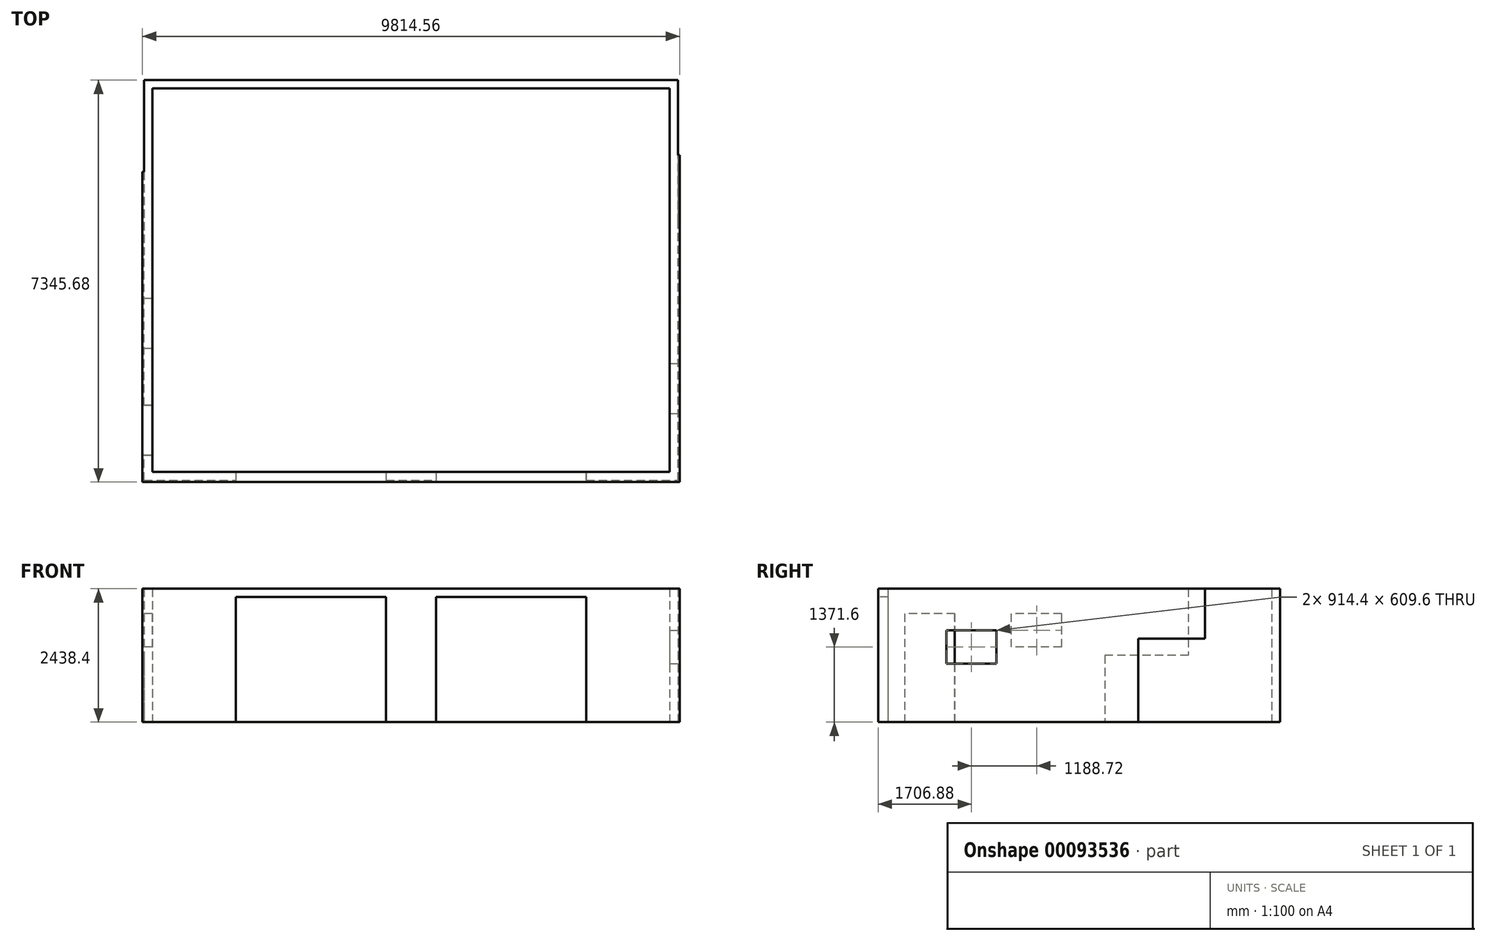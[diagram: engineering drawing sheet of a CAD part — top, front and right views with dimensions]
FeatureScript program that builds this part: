
annotation { "Feature Type Name" : "Feature", "Feature Type Description" : "" }
export const myFeature = defineFeature(function(context is Context, id is Id, definition is map)
    precondition{}
    {
        {
            var Q0;
            Q0=qCreatedBy(makeId("Top.planeOp"),FACE);
            var sketch = newSketch(context, id + "F0", { "sketchPlane" : qUnion([Q0])});
            skLineSegment(sketch, "E0.bottom", {"start": v(0, 0) * mm, "end": v(9753.6, 0) * mm});
            skLineSegment(sketch, "E0.top", {"start": v(0, 7315.2) * mm, "end": v(9753.6, 7315.2) * mm});
            skLineSegment(sketch, "E0.left", {"start": v(0, 0) * mm, "end": v(0, 7315.2) * mm});
            skLineSegment(sketch, "E0.right", {"start": v(9753.6, 0) * mm, "end": v(9753.6, 7315.2) * mm});
            skSolve(sketch);
        }
        {
            var Q0;
            Q0=qSketchRegion(id+"F0",true);
            extrude(context, id + "F1", {"entities" : qUnion([Q0]), "depth" : 304.8 * mm});
        }
        {
            var Q0;
            Q0=makeQuery(id+"F1.opExtrude","CAP_FACE",FACE,{"disambiguationData":[OSD([sQuery(id+"F0.wireOp",EDGE,"E0.bottom"),sQuery(id+"F0.wireOp",EDGE,"E0.top"),sQuery(id+"F0.wireOp",EDGE,"E0.left"),sQuery(id+"F0.wireOp",EDGE,"E0.right")])],"isStart":false});
            var sketch = newSketch(context, id + "F2", { "sketchPlane" : qUnion([Q0])});
            skLineSegment(sketch, "E1.bottom", {"start": v(5334, 0) * mm, "end": v(4419.6, 0) * mm});
            skLineSegment(sketch, "E1.top", {"start": v(5334, 152.4) * mm, "end": v(4419.6, 152.4) * mm});
            skLineSegment(sketch, "E1.left", {"start": v(5334, 0) * mm, "end": v(5334, 152.4) * mm});
            skLineSegment(sketch, "E1.right", {"start": v(4419.6, 0) * mm, "end": v(4419.6, 152.4) * mm});
            skPoint(sketch, "E1.middle", {"position": v(4876.8, 76.2) * mm});
            skLineSegment(sketch, "E2", {"start": v(8077.2, 0) * mm, "end": v(9753.6, 0) * mm});
            skLineSegment(sketch, "E3", {"start": v(9753.6, 0) * mm, "end": v(9753.6, 7315.2) * mm});
            skLineSegment(sketch, "E4", {"start": v(9753.6, 7315.2) * mm, "end": v(0, 7315.2) * mm});
            skLineSegment(sketch, "E5", {"start": v(152.4, 7162.8) * mm, "end": v(9601.2, 7162.8) * mm});
            skLineSegment(sketch, "E6", {"start": v(9601.2, 7162.8) * mm, "end": v(9601.2, 152.4) * mm});
            skLineSegment(sketch, "E7", {"start": v(9601.2, 152.4) * mm, "end": v(8077.2, 152.4) * mm});
            skLineSegment(sketch, "E8", {"start": v(8077.2, 152.4) * mm, "end": v(8077.2, 0) * mm});
            skLineSegment(sketch, "E9", {"start": v(1676.4, 0) * mm, "end": v(1676.4, 152.4) * mm});
            skLineSegment(sketch, "E10", {"start": v(1676.4, 152.4) * mm, "end": v(152.4, 152.4) * mm});
            skLineSegment(sketch, "E11", {"start": v(152.4, 152.4) * mm, "end": v(152.4, 457.2) * mm});
            skLineSegment(sketch, "E12", {"start": v(0, 7315.2) * mm, "end": v(0, 1371.6) * mm});
            skLineSegment(sketch, "E13", {"start": v(0, 0) * mm, "end": v(1676.4, 0) * mm});
            skLineSegment(sketch, "E14", {"start": v(152.4, 457.2) * mm, "end": v(0, 457.2) * mm});
            skLineSegment(sketch, "E15", {"start": v(152.4, 1371.6) * mm, "end": v(0, 1371.6) * mm});
            skLineSegment(sketch, "E16.trimOffspring", {"start": v(152.4, 1371.6) * mm, "end": v(152.4, 7162.8) * mm});
            skLineSegment(sketch, "E17.trimOffspring", {"start": v(0, 457.2) * mm, "end": v(0, 0) * mm});
            skSolve(sketch);
        }
        {
            var Q0;
            Q0=qSketchRegion(id+"F2",true);
            extrude(context, id + "F3", {"entities" : qUnion([Q0]), "operationType" : NewBodyOperationType.ADD, "depth" : 152.4 * mm});
        }
        {
            var Q0;
            Q0=makeQuery(id+"F3.opExtrude","CAP_FACE",FACE,{"disambiguationData":[OSD([sQuery(id+"F2.wireOp",EDGE,"E2"),sQuery(id+"F2.wireOp",EDGE,"E3"),sQuery(id+"F2.wireOp",EDGE,"E4"),sQuery(id+"F2.wireOp",EDGE,"CElO2aeV-4ry8-U5nN-VFw7-lKZjGSDdjc46"),sQuery(id+"F2.wireOp",EDGE,"aXI8KXb9-mfIK-bI9D-YpWg-9FVOQ1UAsdFk"),sQuery(id+"F2.wireOp",EDGE,"YwxrfCe7-5sPB-iO6G-MdUH-hFZLTdnCo4qc"),sQuery(id+"F2.wireOp",EDGE,"E5"),sQuery(id+"F2.wireOp",EDGE,"E6"),sQuery(id+"F2.wireOp",EDGE,"E7"),sQuery(id+"F2.wireOp",EDGE,"E8")])],"isStart":false});
            var sketch = newSketch(context, id + "F4", { "sketchPlane" : qUnion([Q0])});
            skLineSegment(sketch, "E18.3", {"start": v(0, 7162.8) * mm, "end": v(9601.2, 7162.8) * mm});
            skLineSegment(sketch, "E18.4", {"start": v(0, 7315.2) * mm, "end": v(9753.6, 7315.2) * mm});
            skLineSegment(sketch, "E19", {"start": v(9753.6, 7162.8) * mm, "end": v(9753.6, 7315.2) * mm});
            skLineSegment(sketch, "E20", {"start": v(0, 7315.2) * mm, "end": v(0, 7162.8) * mm});
            skLineSegment(sketch, "E21", {"start": v(9601.2, 7162.8) * mm, "end": v(9753.6, 7162.8) * mm});
            skSolve(sketch);
        }
        {
            var Q0;
            Q0=qSketchRegion(id+"F4",true);
            extrude(context, id + "F5", {"entities" : qUnion([Q0]), "operationType" : NewBodyOperationType.ADD, "depth" : 2438.4 * mm});
        }
        {
            var Q0;
            Q0=makeQuery(id+"F5.boolean.opBoolean","MERGE",FACE,{"derivedFrom":[makeQuery(id+"F3.boolean.opBoolean","MERGE",FACE,{"derivedFrom":[makeQuery(id+"F1.opExtrude","SWEPT_FACE",FACE,{"disambiguationData":[OSD([sQuery(id+"F0.wireOp",EDGE,"E0.right")])]}),makeQuery(id+"F3.opExtrude","SWEPT_FACE",FACE,{"disambiguationData":[OSD([sQuery(id+"F2.wireOp",EDGE,"E3")])]})]}),makeQuery(id+"F5.opExtrude","SWEPT_FACE",FACE,{"disambiguationData":[OSD([sQuery(id+"F4.wireOp",EDGE,"E19")])]})]});
            var sketch = newSketch(context, id + "F6", { "sketchPlane" : qUnion([Q0])});
            skLineSegment(sketch, "E22.0", {"start": v(4724.4, 457.2) * mm, "end": v(7162.8, 457.2) * mm});
            skLineSegment(sketch, "E22.1", {"start": v(7162.8, 2895.6) * mm, "end": v(7162.8, 457.2) * mm});
            skLineSegment(sketch, "E23", {"start": v(7162.8, 2895.6) * mm, "end": v(5943.6, 2895.6) * mm});
            skLineSegment(sketch, "E24", {"start": v(5943.6, 2895.6) * mm, "end": v(5943.6, 1981.2) * mm});
            skLineSegment(sketch, "E25", {"start": v(5943.6, 1981.2) * mm, "end": v(4724.4, 1981.2) * mm});
            skLineSegment(sketch, "E26", {"start": v(4724.4, 1981.2) * mm, "end": v(4724.4, 457.2) * mm});
            skPoint(sketch, "E27.orphan", {"position": v(0, 457.2) * mm});
            skSolve(sketch);
        }
        {
            var Q0;
            Q0 = qSketchRegion(id + "F6", true);
            extrude(context, id + "F7", {"entities" : qUnion([Q0]), "operationType" : NewBodyOperationType.ADD, "oppositeDirection" : true, "depth" : 152.4 * mm});
        }
        {
            var Q0;
            Q0=makeQuery(id+"F5.boolean.opBoolean","MERGE",FACE,{"derivedFrom":[makeQuery(id+"F3.boolean.opBoolean","MERGE",FACE,{"derivedFrom":[makeQuery(id+"F1.opExtrude","SWEPT_FACE",FACE,{"disambiguationData":[OSD([sQuery(id+"F0.wireOp",EDGE,"E0.left")])]}),makeQuery(id+"F3.opExtrude","SWEPT_FACE",FACE,{"disambiguationData":[OSD([sQuery(id+"F2.wireOp",EDGE,"E12")])]})]}),makeQuery(id+"F5.opExtrude","SWEPT_FACE",FACE,{"disambiguationData":[OSD([sQuery(id+"F4.wireOp",EDGE,"E20")])]})]});
            var sketch = newSketch(context, id + "F8", { "sketchPlane" : qUnion([Q0])});
            skLineSegment(sketch, "E28.0", {"start": v(-4114.8, 457.2) * mm, "end": v(-7162.8, 457.2) * mm});
            skLineSegment(sketch, "E28.1", {"start": v(-7162.8, 2895.6) * mm, "end": v(-7162.8, 457.2) * mm});
            skLineSegment(sketch, "E29", {"start": v(-7162.8, 2895.6) * mm, "end": v(-5638.8, 2895.6) * mm});
            skLineSegment(sketch, "E30", {"start": v(-5638.8, 2895.6) * mm, "end": v(-5638.8, 1676.4) * mm});
            skLineSegment(sketch, "E31", {"start": v(-5638.8, 1676.4) * mm, "end": v(-4114.8, 1676.4) * mm});
            skLineSegment(sketch, "E32", {"start": v(-4114.8, 1676.4) * mm, "end": v(-4114.8, 457.2) * mm});
            skPoint(sketch, "E33.orphan", {"position": v(-1371.6, 457.2) * mm});
            skSolve(sketch);
        }
        {
            var Q0;
            Q0 = qSketchRegion(id + "F8", true);
            extrude(context, id + "F9", {"entities" : qUnion([Q0]), "operationType" : NewBodyOperationType.ADD, "oppositeDirection" : true, "depth" : 152.4 * mm});
        }
        {
            var Q0;
            Q0=makeQuery(id+"F5.boolean.opBoolean","MERGE",FACE,{"derivedFrom":[makeQuery(id+"F3.boolean.opBoolean","MERGE",FACE,{"derivedFrom":[makeQuery(id+"F1.opExtrude","SWEPT_FACE",FACE,{"disambiguationData":[OSD([sQuery(id+"F0.wireOp",EDGE,"E0.right")])]}),makeQuery(id+"F3.opExtrude","SWEPT_FACE",FACE,{"disambiguationData":[OSD([sQuery(id+"F2.wireOp",EDGE,"E3")])]})]}),makeQuery(id+"F5.opExtrude","SWEPT_FACE",FACE,{"disambiguationData":[OSD([sQuery(id+"F4.wireOp",EDGE,"E19")])]})]});
            var sketch = newSketch(context, id + "F10", { "sketchPlane" : qUnion([Q0])});
            skLineSegment(sketch, "E34.0", {"start": v(5943.6, 2895.6) * mm, "end": v(5943.6, 1981.2) * mm});
            skLineSegment(sketch, "E34.1", {"start": v(5943.6, 1981.2) * mm, "end": v(4724.4, 1981.2) * mm});
            skLineSegment(sketch, "E34.2", {"start": v(4724.4, 1981.2) * mm, "end": v(4724.4, 457.2) * mm});
            skLineSegment(sketch, "E34.3", {"start": v(0, 457.2) * mm, "end": v(4724.4, 457.2) * mm});
            skLineSegment(sketch, "E35", {"start": v(5943.6, 2895.6) * mm, "end": v(0, 2895.6) * mm});
            skLineSegment(sketch, "E36", {"start": v(0, 2895.6) * mm, "end": v(0, 457.2) * mm});
            skPoint(sketch, "E37.orphan", {"position": v(5943.6, 457.2) * mm});
            skLineSegment(sketch, "E38.bottom", {"start": v(1219.2, 2133.6) * mm, "end": v(2133.6, 2133.6) * mm});
            skLineSegment(sketch, "E38.top", {"start": v(1219.2, 1524) * mm, "end": v(2133.6, 1524) * mm});
            skLineSegment(sketch, "E38.left", {"start": v(1219.2, 2133.6) * mm, "end": v(1219.2, 1524) * mm});
            skLineSegment(sketch, "E38.right", {"start": v(2133.6, 2133.6) * mm, "end": v(2133.6, 1524) * mm});
            skSolve(sketch);
        }
        {
            var Q0;
            Q0 = qSketchRegion(id + "F10", true);
            extrude(context, id + "F11", {"entities" : qUnion([Q0]), "oppositeDirection" : true, "depth" : 152.4 * mm, "hasSecondDirection" : true, "secondDirectionOppositeDirection" : false, "secondDirectionDepth" : 30.48 * mm});
        }
        {
            var Q0;
            Q0=makeQuery(id+"F3.boolean.opBoolean","MERGE",FACE,{"derivedFrom":[makeQuery(id+"F1.opExtrude","SWEPT_FACE",FACE,{"disambiguationData":[OSD([sQuery(id+"F0.wireOp",EDGE,"E0.bottom")])]}),makeQuery(id+"F3.opExtrude","SWEPT_FACE",FACE,{"disambiguationData":[OSD([sQuery(id+"F2.wireOp",EDGE,"E1.bottom")])]}),makeQuery(id+"F3.opExtrude","SWEPT_FACE",FACE,{"disambiguationData":[OSD([sQuery(id+"F2.wireOp",EDGE,"E2")])]}),makeQuery(id+"F3.opExtrude","SWEPT_FACE",FACE,{"disambiguationData":[OSD([sQuery(id+"F2.wireOp",EDGE,"E13")])]})]});
            var sketch = newSketch(context, id + "F12", { "sketchPlane" : qUnion([Q0])});
            skLineSegment(sketch, "E39.0", {"start": v(0, 457.2) * mm, "end": v(1676.4, 457.2) * mm});
            skLineSegment(sketch, "E39.2", {"start": v(4419.6, 457.2) * mm, "end": v(5334, 457.2) * mm});
            skLineSegment(sketch, "E39.3", {"start": v(8077.2, 457.2) * mm, "end": v(9753.6, 457.2) * mm});
            skLineSegment(sketch, "E39.4", {"start": v(9601.2, 457.2) * mm, "end": v(9784.08, 457.2) * mm});
            skLineSegment(sketch, "E40.1", {"start": v(9784.08, 2895.6) * mm, "end": v(9784.08, 457.2) * mm});
            skLineSegment(sketch, "E41", {"start": v(1676.4, 457.2) * mm, "end": v(1676.4, 2743.2) * mm});
            skLineSegment(sketch, "E42", {"start": v(1676.4, 2743.2) * mm, "end": v(4419.6, 2743.2) * mm});
            skLineSegment(sketch, "E43", {"start": v(4419.6, 2743.2) * mm, "end": v(4419.6, 457.2) * mm});
            skLineSegment(sketch, "E44", {"start": v(5334, 457.2) * mm, "end": v(5334, 2743.2) * mm});
            skLineSegment(sketch, "E45", {"start": v(5334, 2743.2) * mm, "end": v(8077.2, 2743.2) * mm});
            skLineSegment(sketch, "E46", {"start": v(8077.2, 2743.2) * mm, "end": v(8077.2, 457.2) * mm});
            skLineSegment(sketch, "E47", {"start": v(0, 457.2) * mm, "end": v(-30.48, 457.2) * mm});
            skLineSegment(sketch, "E48", {"start": v(-30.48, 457.2) * mm, "end": v(-30.48, 2895.6) * mm});
            skLineSegment(sketch, "E49.0", {"start": v(152.4, 2895.6) * mm, "end": v(9601.2, 2895.6) * mm});
            skLineSegment(sketch, "E50.0", {"start": v(9601.2, 2895.6) * mm, "end": v(9784.08, 2895.6) * mm});
            skLineSegment(sketch, "E51", {"start": v(-30.48, 2895.6) * mm, "end": v(152.4, 2895.6) * mm});
            skSolve(sketch);
        }
        {
            var Q0;
            Q0 = qSketchRegion(id + "F12", true);
            extrude(context, id + "F13", {"entities" : qUnion([Q0]), "operationType" : NewBodyOperationType.ADD, "oppositeDirection" : true, "depth" : 152.4 * mm, "hasSecondDirection" : true, "secondDirectionOppositeDirection" : false, "secondDirectionDepth" : 30.48 * mm});
        }
        {
            var Q0;
            Q0=makeQuery(id+"F13.opExtrude","SWEPT_FACE",FACE,{"disambiguationData":[OSD([sQuery(id+"F12.wireOp",EDGE,"E48")])]});
            var sketch = newSketch(context, id + "F14", { "sketchPlane" : qUnion([Q0])});
            skLineSegment(sketch, "E52.0", {"start": v(-5638.8, 2895.6) * mm, "end": v(-5638.8, 1676.4) * mm});
            skLineSegment(sketch, "E52.1", {"start": v(-5638.8, 1676.4) * mm, "end": v(-4114.8, 1676.4) * mm});
            skLineSegment(sketch, "E52.2", {"start": v(-4114.8, 1676.4) * mm, "end": v(-4114.8, 457.2) * mm});
            skLineSegment(sketch, "E52.3", {"start": v(-1371.6, 457.2) * mm, "end": v(-4114.8, 457.2) * mm});
            skLineSegment(sketch, "E52.4", {"start": v(30.48, 457.2) * mm, "end": v(30.48, 2895.6) * mm});
            skLineSegment(sketch, "E53", {"start": v(-5638.8, 2895.6) * mm, "end": v(30.48, 2895.6) * mm});
            skLineSegment(sketch, "E54.bottom", {"start": v(-3322.32, 1828.8) * mm, "end": v(-2407.92, 1828.8) * mm});
            skLineSegment(sketch, "E54.top", {"start": v(-3322.32, 2438.4) * mm, "end": v(-2407.92, 2438.4) * mm});
            skLineSegment(sketch, "E54.left", {"start": v(-3322.32, 1828.8) * mm, "end": v(-3322.32, 2438.4) * mm});
            skLineSegment(sketch, "E54.right", {"start": v(-2407.92, 1828.8) * mm, "end": v(-2407.92, 2438.4) * mm});
            skLineSegment(sketch, "E55", {"start": v(-1371.6, 457.2) * mm, "end": v(-1371.6, 2438.4) * mm});
            skLineSegment(sketch, "E56", {"start": v(-1371.6, 2438.4) * mm, "end": v(-457.2, 2438.4) * mm});
            skLineSegment(sketch, "E57", {"start": v(-457.2, 2438.4) * mm, "end": v(-457.2, 457.2) * mm});
            skPoint(sketch, "E58.0.end.orphan", {"position": v(-1371.6, 304.8) * mm});
            skPoint(sketch, "E58.0.start.orphan", {"position": v(-1371.6, 457.2) * mm});
            skPoint(sketch, "E58.1.end.orphan", {"position": v(-457.2, 304.8) * mm});
            skLineSegment(sketch, "E59", {"start": v(-457.2, 457.2) * mm, "end": v(30.48, 457.2) * mm});
            skSolve(sketch);
        }
        {
            var Q0;
            Q0 = qSketchRegion(id + "F14", true);
            extrude(context, id + "F15", {"entities" : qUnion([Q0]), "operationType" : NewBodyOperationType.ADD, "oppositeDirection" : true, "depth" : 182.88 * mm});
        }
        {
            var Q0;
            Q0=makeQuery(id+"F1.opExtrude","CAP_FACE",FACE,{"disambiguationData":[OSD([sQuery(id+"F0.wireOp",EDGE,"E0.bottom"),sQuery(id+"F0.wireOp",EDGE,"E0.top"),sQuery(id+"F0.wireOp",EDGE,"E0.left"),sQuery(id+"F0.wireOp",EDGE,"E0.right")])],"isStart":true});
            var sketch = newSketch(context, id + "F16", { "sketchPlane" : qUnion([Q0])});
            skLineSegment(sketch, "E60.bottom", {"start": v(0, 0) * mm, "end": v(9753.6, 0) * mm});
            skLineSegment(sketch, "E60.top", {"start": v(0, -7315.2) * mm, "end": v(9753.6, -7315.2) * mm});
            skLineSegment(sketch, "E60.left", {"start": v(0, 0) * mm, "end": v(0, -7315.2) * mm});
            skLineSegment(sketch, "E60.right", {"start": v(9753.6, 0) * mm, "end": v(9753.6, -7315.2) * mm});
            skSolve(sketch);
        }
        {
            var Q0;
            Q0 = qSketchRegion(id + "F16", true);
            extrude(context, id + "F17", {"entities" : qUnion([Q0]), "operationType" : NewBodyOperationType.REMOVE, "oppositeDirection" : true, "depth" : 457.5 * mm});
        }
    });
